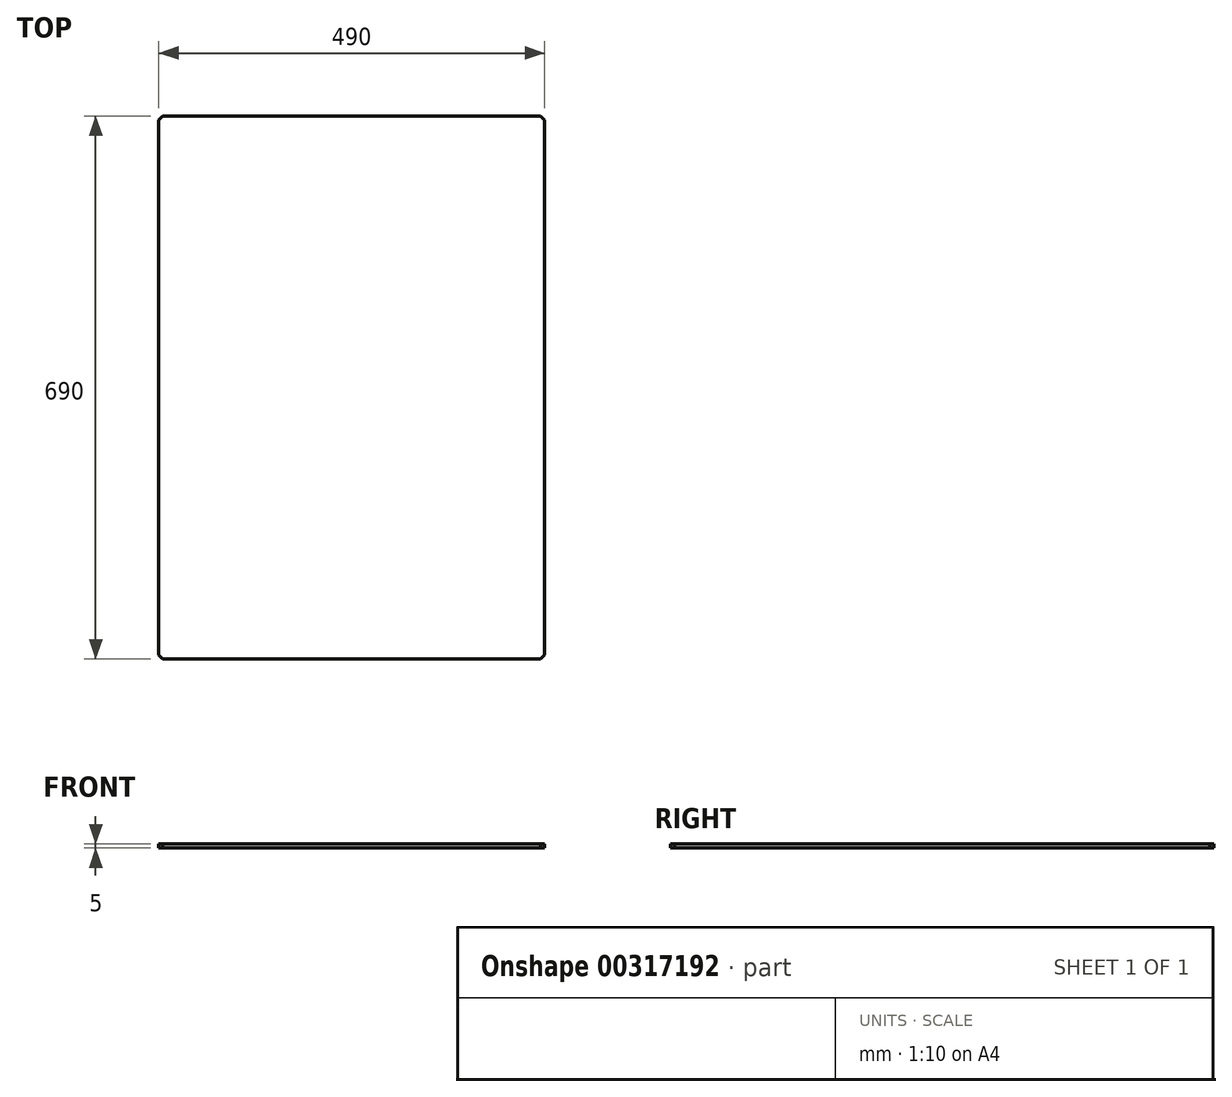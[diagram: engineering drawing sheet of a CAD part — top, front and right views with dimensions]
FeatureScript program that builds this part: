
annotation { "Feature Type Name" : "Feature", "Feature Type Description" : "" }
export const myFeature = defineFeature(function(context is Context, id is Id, definition is map)
    precondition{}
    {
        {
            var Q0;
            Q0=qCreatedBy(makeId("Front.planeOp"),FACE);
            var sketch = newSketch(context, id + "F0", { "sketchPlane" : qUnion([Q0])});
            skLineSegment(sketch, "E0", {"start": v(-245, 0) * mm, "end": v(245, 0) * mm});
            skLineSegment(sketch, "E1", {"start": v(-245, 5) * mm, "end": v(245, 5) * mm});
            skLineSegment(sketch, "E2", {"start": v(-245, 0) * mm, "end": v(-245, 5) * mm});
            skLineSegment(sketch, "E3", {"start": v(245, 5) * mm, "end": v(245, 0) * mm});
            skSolve(sketch);
        }
        {
            var Q0;
            Q0 = qSketchRegion(id + "F0", true);
            var Q1;
            Q1 = qConstructionFilter(qBodyType(qCreatedBy(id + "F0" ,EDGE), BodyType.WIRE), ConstructionObject.NO);
            extrude(context, id + "F1", {"entities" : qUnion([Q0]), "surfaceEntities" : qUnion([Q1]), "depth" : 345 * mm, "hasSecondDirection" : true, "secondDirectionOppositeDirection" : true, "secondDirectionDepth" : 345 * mm});
        }
        {
            var Q0;
            Q0=makeQuery(id+"F1.opExtrude","CAP_EDGE",EDGE,{"disambiguationData":[OSD([sQuery(id+"F0.wireOp",EDGE,"E3")])],"isStart":false});
            var Q1;
            Q1=makeQuery(id+"F1.opExtrude","CAP_EDGE",EDGE,{"disambiguationData":[OSD([sQuery(id+"F0.wireOp",EDGE,"E3")])],"isStart":true});
            var Q2;
            Q2=makeQuery(id+"F1.opExtrude","CAP_EDGE",EDGE,{"disambiguationData":[OSD([sQuery(id+"F0.wireOp",EDGE,"E2")])],"isStart":true});
            var Q3;
            Q3=makeQuery(id+"F1.opExtrude","CAP_EDGE",EDGE,{"disambiguationData":[OSD([sQuery(id+"F0.wireOp",EDGE,"E2")])],"isStart":false});
            chamfer(context, id + "F2", {"entities" : qUnion([Q0, Q1, Q2, Q3]), "width" : 5 * mm, "tangentPropagation" : true});
        }
    });
